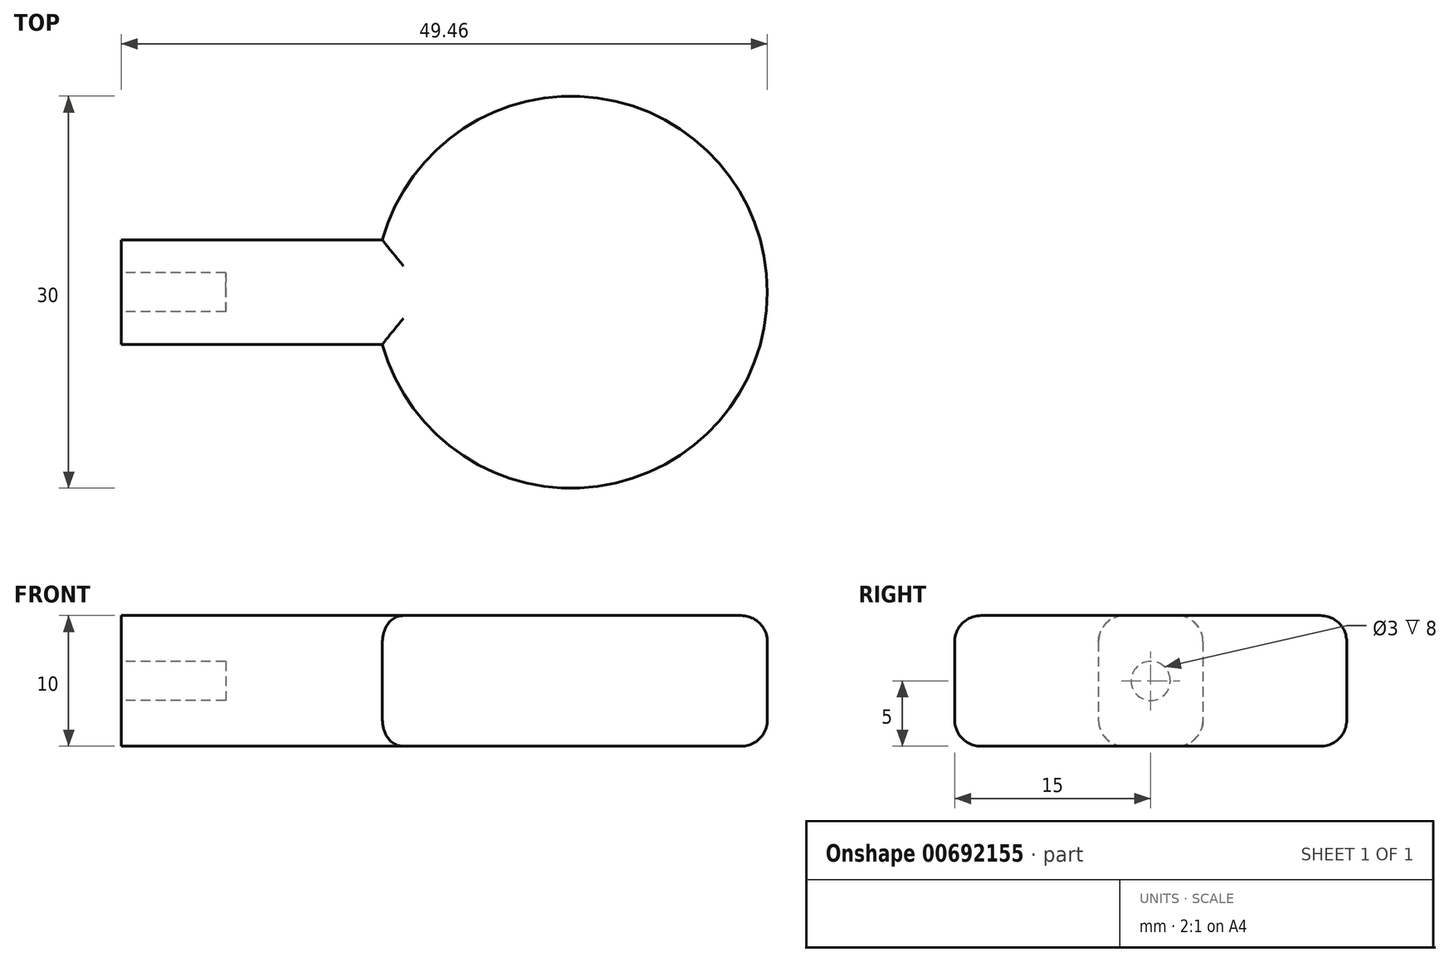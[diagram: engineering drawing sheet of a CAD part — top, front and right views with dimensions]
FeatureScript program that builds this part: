
annotation { "Feature Type Name" : "Feature", "Feature Type Description" : "" }
export const myFeature = defineFeature(function(context is Context, id is Id, definition is map)
    precondition{}
    {
        {
            var Q0;
            Q0=qCreatedBy(makeId("Top.planeOp"),FACE);
            var sketch = newSketch(context, id + "F0", { "sketchPlane" : qUnion([Q0])});
            skCircle(sketch, "E0", {"center": v(0, 0) * mm, "radius": 15 * mm});
            skLineSegment(sketch, "E1", {"start": v(-14.46, 4) * mm, "end": v(-34.46, 4) * mm});
            skLineSegment(sketch, "E2", {"start": v(0, 0) * mm, "end": v(-79.82, 0) * mm, "construction": true});
            skLineSegment(sketch, "E3", {"start": v(-21.13, 4) * mm, "end": v(-21.13, 0) * mm, "construction": true});
            skLineSegment(sketch, "E4", {"start": v(-21.13, 0) * mm, "end": v(-21.13, -4) * mm, "construction": true});
            skLineSegment(sketch, "E5", {"start": v(-34.46, 4) * mm, "end": v(-34.46, -7.96) * mm, "construction": true});
            skLineSegment(sketch, "E6", {"start": v(-21.13, -4) * mm, "end": v(-34.46, -4) * mm});
            skLineSegment(sketch, "E7", {"start": v(-34.46, -4) * mm, "end": v(-34.46, 4) * mm});
            skLineSegment(sketch, "E8", {"start": v(-21.13, -4) * mm, "end": v(-14.46, -4) * mm});
            skSolve(sketch);
        }
        {
            var Q0;
            Q0 = qSketchRegion(id + "F0", true);
            extrude(context, id + "F1", {"entities" : qUnion([Q0]), "depth" : 10 * mm, "offsetDistance" : 25 * mm});
        }
        {
            var Q0;
            Q0=makeQuery(id+"F1.opExtrude","CAP_EDGE",EDGE,{"disambiguationData":[OSD([sQuery(id+"F0.wireOp",EDGE,"E0")])],"isStart":false});
            var Q1;
            Q1=makeQuery(id+"F1.opExtrude","CAP_EDGE",EDGE,{"disambiguationData":[OSD([sQuery(id+"F0.wireOp",EDGE,"E1")])],"isStart":false});
            var Q2;
            Q2=makeQuery(id+"F1.opExtrude","CAP_EDGE",EDGE,{"disambiguationData":[OSD([sQuery(id+"F0.wireOp",EDGE,"E0")])],"isStart":true});
            var Q3;
            Q3=makeQuery(id+"F1.opExtrude","CAP_EDGE",EDGE,{"disambiguationData":[OSD([sQuery(id+"F0.wireOp",EDGE,"E1")])],"isStart":true});
            fillet(context, id + "F2", {"entities" : qUnion([Q0, Q1, Q2, Q3]), "radius" : 2 * mm, "tangentPropagation" : true, "allowEdgeOverflow" : false});
        }
        {
            var Q0;
            Q0=makeQuery(id+"F1.opExtrude","CAP_EDGE",EDGE,{"disambiguationData":[OSD([sQuery(id+"F0.wireOp",EDGE,"E6"),sQuery(id+"F0.wireOp",EDGE,"E8")])],"isStart":false});
            var Q1;
            Q1=makeQuery(id+"F1.opExtrude","CAP_EDGE",EDGE,{"disambiguationData":[OSD([sQuery(id+"F0.wireOp",EDGE,"E6"),sQuery(id+"F0.wireOp",EDGE,"E8")])],"isStart":true});
            fillet(context, id + "F3", {"entities" : qUnion([Q0, Q1]), "radius" : 2 * mm, "tangentPropagation" : true, "allowEdgeOverflow" : false});
        }
        {
            var Q0;
            Q0=makeQuery(id+"F1.opExtrude","SWEPT_FACE",FACE,{"disambiguationData":[OSD([sQuery(id+"F0.wireOp",EDGE,"E7")])]});
            var sketch = newSketch(context, id + "F4", { "sketchPlane" : qUnion([Q0])});
            skLineSegment(sketch, "E9", {"start": v(0, 10) * mm, "end": v(0, 0) * mm, "construction": true});
            skCircle(sketch, "E10", {"center": v(0, 5) * mm, "radius": 1.5 * mm});
            skSolve(sketch);
        }
        {
            var Q0;
            Q0 = qSketchRegion(id + "F4", true);
            extrude(context, id + "F5", {"entities" : qUnion([Q0]), "operationType" : NewBodyOperationType.REMOVE, "oppositeDirection" : true, "depth" : 8 * mm, "offsetDistance" : 25 * mm});
        }
    });
